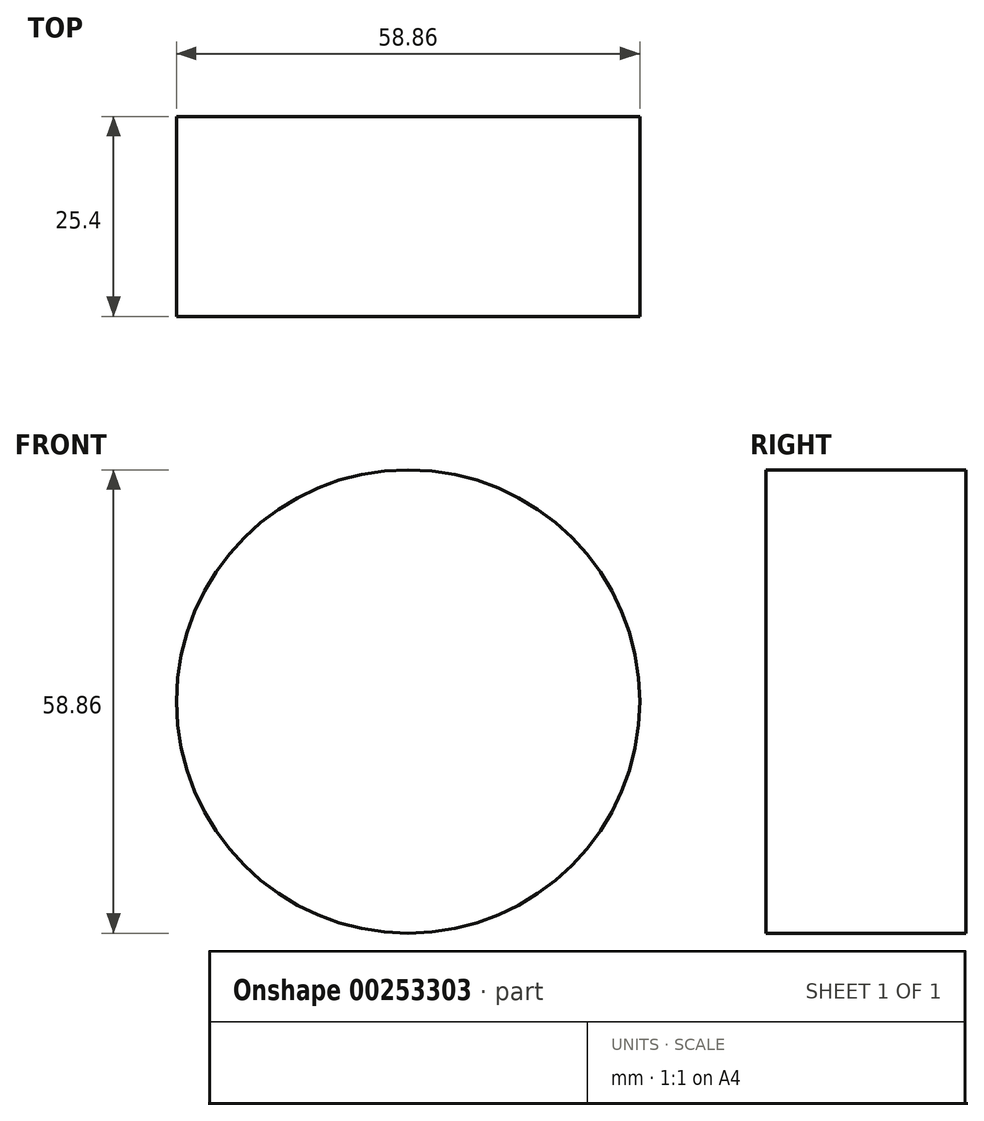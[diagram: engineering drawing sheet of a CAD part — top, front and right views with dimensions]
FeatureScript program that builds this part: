
annotation { "Feature Type Name" : "Feature", "Feature Type Description" : "" }
export const myFeature = defineFeature(function(context is Context, id is Id, definition is map)
    precondition{}
    {
        {
            var Q0;
            Q0=qCreatedBy(makeId("Front.planeOp"),FACE);
            var sketch = newSketch(context, id + "F0", { "sketchPlane" : qUnion([Q0])});
            skCircle(sketch, "E0", {"center": v(0, 0) * mm, "radius": 29.43 * mm});
            skSolve(sketch);
        }
        {
            var Q0;
            Q0 = qSketchRegion(id + "F0", true);
            extrude(context, id + "F1", {"entities" : qUnion([Q0]), "depth" : 25.4 * mm});
        }
    });
